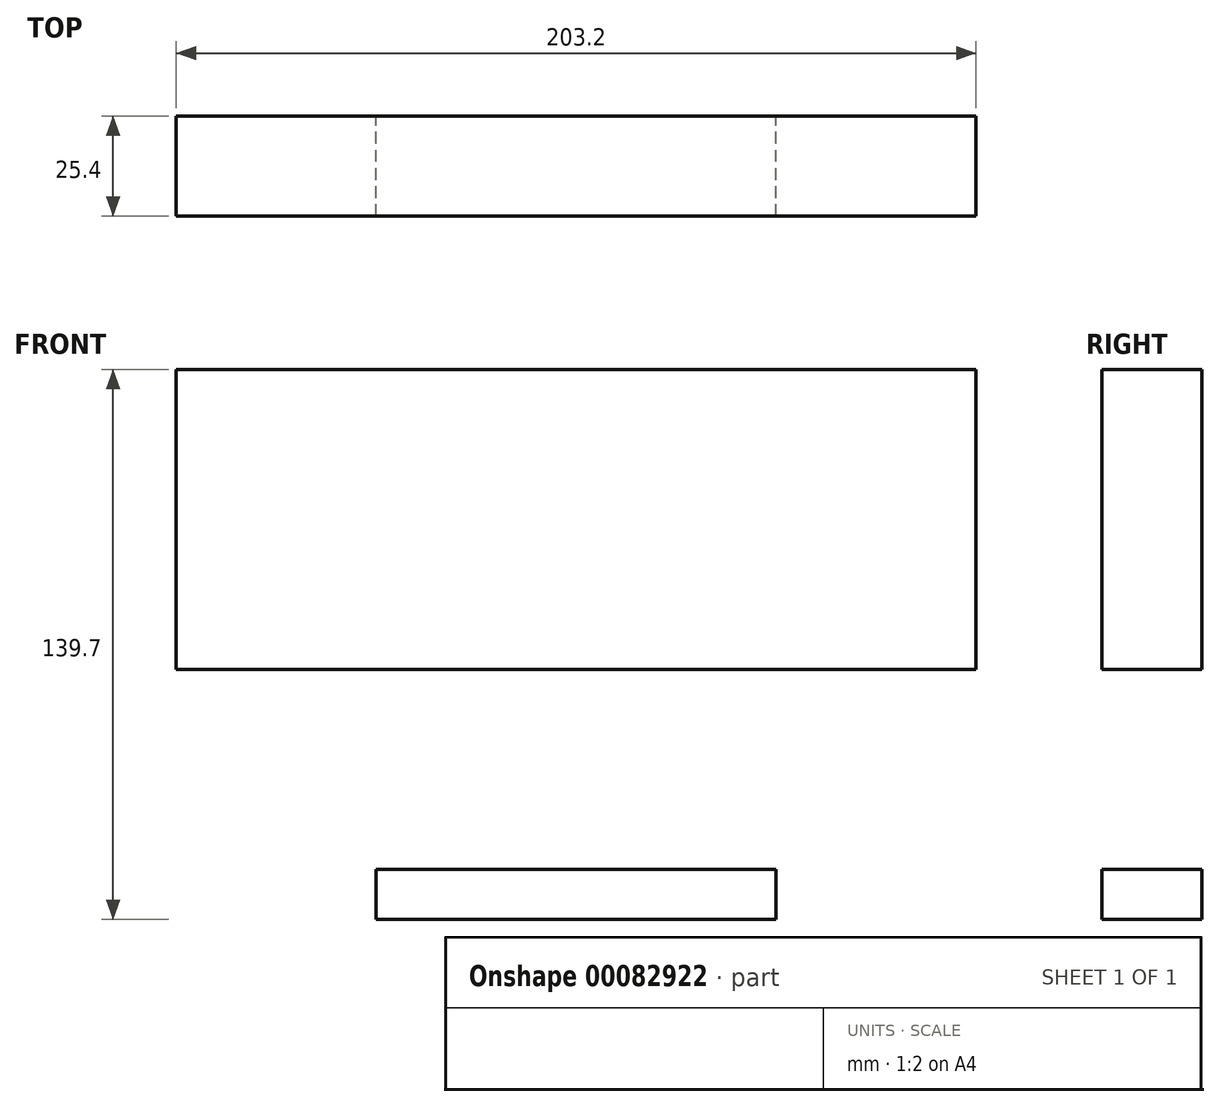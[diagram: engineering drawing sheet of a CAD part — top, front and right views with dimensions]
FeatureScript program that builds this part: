
annotation { "Feature Type Name" : "Feature", "Feature Type Description" : "" }
export const myFeature = defineFeature(function(context is Context, id is Id, definition is map)
    precondition{}
    {
        {
            var Q0;
            Q0=qCreatedBy(makeId("Front.planeOp"),FACE);
            var sketch = newSketch(context, id + "F0", { "sketchPlane" : qUnion([Q0])});
            skLineSegment(sketch, "E0.bottom", {"start": v(-101.6, 38.1) * mm, "end": v(101.6, 38.1) * mm});
            skLineSegment(sketch, "E0.top", {"start": v(-101.6, -38.1) * mm, "end": v(101.6, -38.1) * mm});
            skLineSegment(sketch, "E0.left", {"start": v(-101.6, 38.1) * mm, "end": v(-101.6, -38.1) * mm});
            skLineSegment(sketch, "E0.right", {"start": v(101.6, 38.1) * mm, "end": v(101.6, -38.1) * mm});
            skPoint(sketch, "E0.middle", {"position": v(0, 0) * mm});
            skLineSegment(sketch, "E1.bottom", {"start": v(-25.4, -88.9) * mm, "end": v(25.4, -88.9) * mm});
            skLineSegment(sketch, "E1.top", {"start": v(-25.4, -38.1) * mm, "end": v(25.4, -38.1) * mm});
            skLineSegment(sketch, "E1.left", {"start": v(-25.4, -88.9) * mm, "end": v(-25.4, -38.1) * mm});
            skLineSegment(sketch, "E1.right", {"start": v(25.4, -88.9) * mm, "end": v(25.4, -38.1) * mm});
            skPoint(sketch, "E1.middle", {"position": v(0, -63.5) * mm});
            skLineSegment(sketch, "E2.bottom", {"start": v(-50.8, -88.9) * mm, "end": v(50.8, -88.9) * mm});
            skLineSegment(sketch, "E2.top", {"start": v(-50.8, -101.6) * mm, "end": v(50.8, -101.6) * mm});
            skLineSegment(sketch, "E2.left", {"start": v(-50.8, -88.9) * mm, "end": v(-50.8, -101.6) * mm});
            skLineSegment(sketch, "E2.right", {"start": v(50.8, -88.9) * mm, "end": v(50.8, -101.6) * mm});
            skPoint(sketch, "E2.middle", {"position": v(0, -95.25) * mm});
            skSolve(sketch);
        }
        {
            var Q0;
            Q0=makeQuery(id+"F0.imprint","IMPRINT",FACE,{"disambiguationData":[TD([[makeQuery(id+"F0.imprint","IMPRINT",EDGE,{"derivedFrom":sQuery(id+"F0.wireOp",EDGE,"E0.bottom")}),-1.0]])]});
            var Q1;
            Q1=makeQuery(id+"F0.imprint","IMPRINT",FACE,{"disambiguationData":[TD([[makeQuery(id+"F0.imprint","IMPRINT",EDGE,{"derivedFrom":sQuery(id+"F0.wireOp",EDGE,"E2.top")}),1.0]])]});
            var Q2;
            Q2=makeQuery(id+"F0.imprint","IMPRINT",FACE,{"disambiguationData":[TD([[makeQuery(id+"F0.imprint","IMPRINT",EDGE,{"derivedFrom":sQuery(id+"F0.wireOp",EDGE,"E1.top")}),-1.0]])]});
            extrude(context, id + "F1", {"entities" : qUnion([Q0, Q1, Q2]), "depth" : 25.4 * mm});
        }
    });
